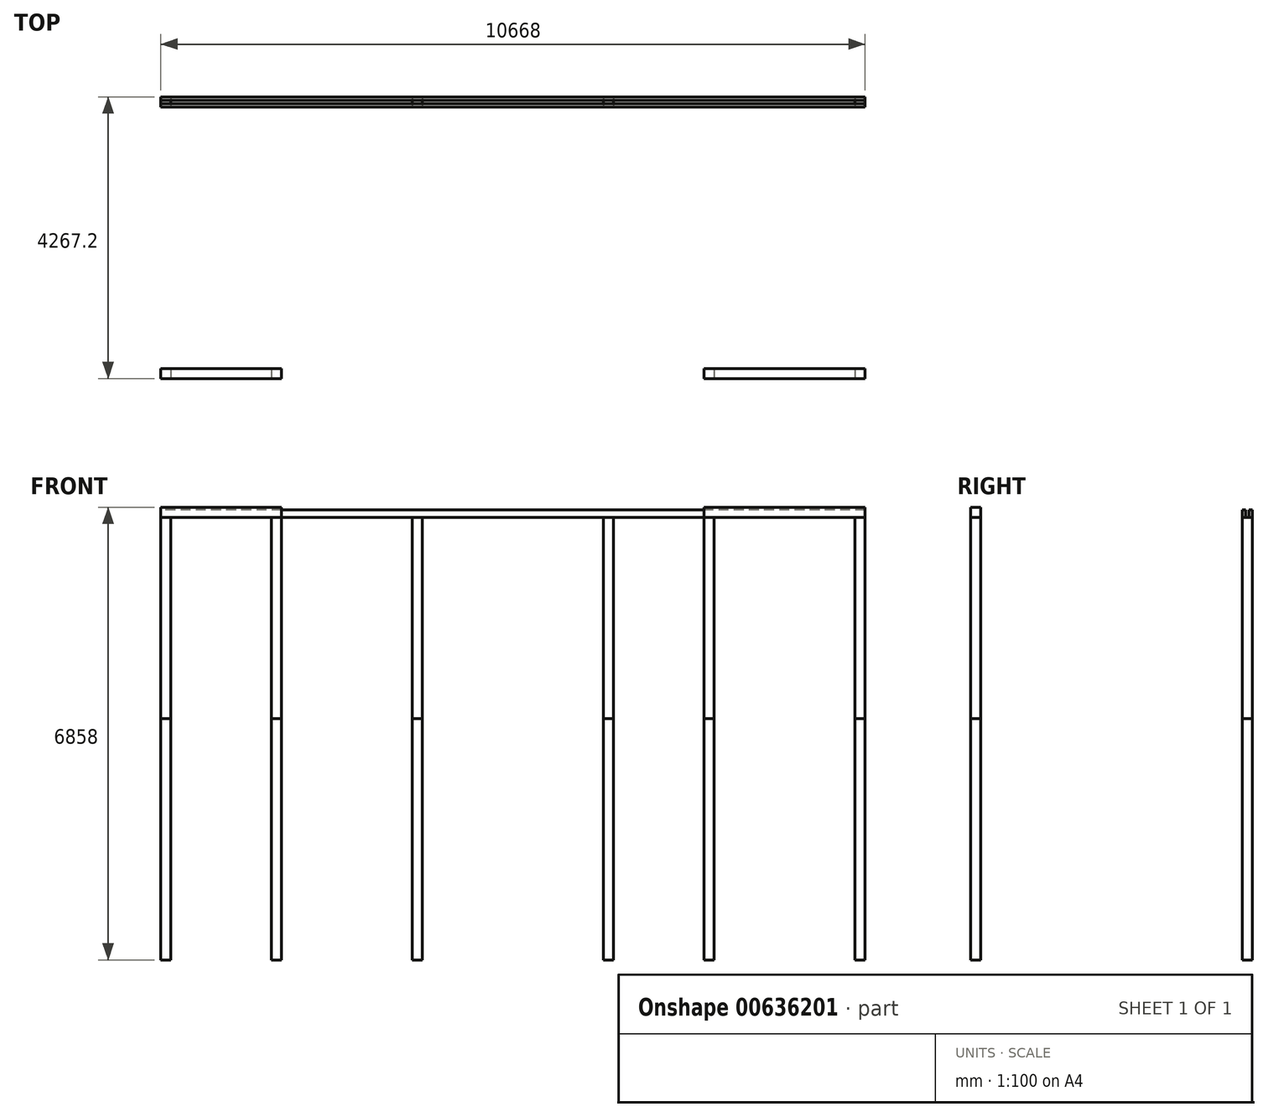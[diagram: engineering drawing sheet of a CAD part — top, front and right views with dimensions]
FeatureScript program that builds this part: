
annotation { "Feature Type Name" : "Feature", "Feature Type Description" : "" }
export const myFeature = defineFeature(function(context is Context, id is Id, definition is map)
    precondition{}
    {
        {
            var Q0;
            Q0=qCreatedBy(makeId("Top.planeOp"),FACE);
            var sketch = newSketch(context, id + "F0", { "sketchPlane" : qUnion([Q0])});
            skLineSegment(sketch, "E0.bottom", {"start": v(-152.4, 4130.06) * mm, "end": v(0, 4130.06) * mm});
            skLineSegment(sketch, "E0.top", {"start": v(-152.4, 3977.66) * mm, "end": v(0, 3977.66) * mm});
            skLineSegment(sketch, "E0.left", {"start": v(-152.4, 4130.06) * mm, "end": v(-152.4, 3977.66) * mm});
            skLineSegment(sketch, "E0.right", {"start": v(0, 4130.06) * mm, "end": v(0, 3977.66) * mm});
            skLineSegment(sketch, "E1.bottom", {"start": v(3657.6, 4130.06) * mm, "end": v(3810, 4130.06) * mm});
            skLineSegment(sketch, "E1.top", {"start": v(3657.6, 3977.66) * mm, "end": v(3810, 3977.66) * mm});
            skLineSegment(sketch, "E1.left", {"start": v(3657.6, 4130.06) * mm, "end": v(3657.6, 3977.66) * mm});
            skLineSegment(sketch, "E1.right", {"start": v(3810, 4130.06) * mm, "end": v(3810, 3977.66) * mm});
            skLineSegment(sketch, "E2.bottom", {"start": v(6553.2, 4130.06) * mm, "end": v(6705.6, 4130.06) * mm});
            skLineSegment(sketch, "E2.top", {"start": v(6553.2, 3977.66) * mm, "end": v(6705.6, 3977.66) * mm});
            skLineSegment(sketch, "E2.left", {"start": v(6553.2, 4130.06) * mm, "end": v(6553.2, 3977.66) * mm});
            skLineSegment(sketch, "E2.right", {"start": v(6705.6, 4130.06) * mm, "end": v(6705.6, 3977.66) * mm});
            skLineSegment(sketch, "E3.bottom", {"start": v(-152.4, 15.26) * mm, "end": v(0, 15.26) * mm});
            skLineSegment(sketch, "E3.top", {"start": v(-152.4, -137.14) * mm, "end": v(0, -137.14) * mm});
            skLineSegment(sketch, "E3.left", {"start": v(-152.4, 15.26) * mm, "end": v(-152.4, -137.14) * mm});
            skLineSegment(sketch, "E3.right", {"start": v(0, 15.26) * mm, "end": v(0, -137.14) * mm});
            skLineSegment(sketch, "E4.bottom", {"start": v(1524, 15.26) * mm, "end": v(1676.4, 15.26) * mm});
            skLineSegment(sketch, "E4.top", {"start": v(1524, -137.14) * mm, "end": v(1676.4, -137.14) * mm});
            skLineSegment(sketch, "E4.left", {"start": v(1524, 15.26) * mm, "end": v(1524, -137.14) * mm});
            skLineSegment(sketch, "E4.right", {"start": v(1676.4, 15.26) * mm, "end": v(1676.4, -137.14) * mm});
            skLineSegment(sketch, "E5.bottom", {"start": v(8077.2, 15.26) * mm, "end": v(8229.6, 15.26) * mm});
            skLineSegment(sketch, "E5.top", {"start": v(8077.2, -137.14) * mm, "end": v(8229.6, -137.14) * mm});
            skLineSegment(sketch, "E5.left", {"start": v(8077.2, 15.26) * mm, "end": v(8077.2, -137.14) * mm});
            skLineSegment(sketch, "E5.right", {"start": v(8229.6, 15.26) * mm, "end": v(8229.6, -137.14) * mm});
            skLineSegment(sketch, "E6.bottom", {"start": v(10363.2, 4130.06) * mm, "end": v(10515.6, 4130.06) * mm});
            skLineSegment(sketch, "E6.top", {"start": v(10363.2, 3977.66) * mm, "end": v(10515.6, 3977.66) * mm});
            skLineSegment(sketch, "E6.left", {"start": v(10363.2, 4130.06) * mm, "end": v(10363.2, 3977.66) * mm});
            skLineSegment(sketch, "E6.right", {"start": v(10515.6, 4130.06) * mm, "end": v(10515.6, 3977.66) * mm});
            skLineSegment(sketch, "E7.bottom", {"start": v(10363.2, 15.26) * mm, "end": v(10515.6, 15.26) * mm});
            skLineSegment(sketch, "E7.top", {"start": v(10363.2, -137.14) * mm, "end": v(10515.6, -137.14) * mm});
            skLineSegment(sketch, "E7.left", {"start": v(10363.2, 15.26) * mm, "end": v(10363.2, -137.14) * mm});
            skLineSegment(sketch, "E7.right", {"start": v(10515.6, 15.26) * mm, "end": v(10515.6, -137.14) * mm});
            skSolve(sketch);
        }
        {
            var Q0;
            Q0 = qSketchRegion(id + "F0", true);
            extrude(context, id + "F1", {"entities" : qUnion([Q0]), "depth" : 3048 * mm, "offsetDistance" : 25.4 * mm});
        }
        {
            var Q0;
            Q0 = qSketchRegion(id + "F0", true);
            extrude(context, id + "F2", {"entities" : qUnion([Q0]), "oppositeDirection" : true, "depth" : 3657.6 * mm, "offsetDistance" : 25.4 * mm});
        }
        {
            var Q0;
            Q0=makeQuery(id+"F1.opExtrude","SWEPT_FACE",FACE,{"disambiguationData":[OSD([sQuery(id+"F0.wireOp",EDGE,"E3.left")])]});
            var sketch = newSketch(context, id + "F3", { "sketchPlane" : qUnion([Q0])});
            skLineSegment(sketch, "E8.bottom", {"start": v(-15.26, 3048) * mm, "end": v(137.14, 3048) * mm});
            skLineSegment(sketch, "E8.top", {"start": v(-15.26, 3200.4) * mm, "end": v(137.14, 3200.4) * mm});
            skLineSegment(sketch, "E8.left", {"start": v(-15.26, 3048) * mm, "end": v(-15.26, 3200.4) * mm});
            skLineSegment(sketch, "E8.right", {"start": v(137.14, 3048) * mm, "end": v(137.14, 3200.4) * mm});
            skLineSegment(sketch, "E9.bottom", {"start": v(-4129.63, 3048.56) * mm, "end": v(-4078.83, 3048.56) * mm});
            skLineSegment(sketch, "E9.top", {"start": v(-4129.63, 3162.86) * mm, "end": v(-4078.83, 3162.86) * mm});
            skLineSegment(sketch, "E9.left", {"start": v(-4129.63, 3048.56) * mm, "end": v(-4129.63, 3162.86) * mm});
            skLineSegment(sketch, "E9.right", {"start": v(-4078.83, 3048.56) * mm, "end": v(-4078.83, 3162.86) * mm});
            skLineSegment(sketch, "E10", {"start": v(-3977.66, 3048) * mm, "end": v(-3977.66, 3162.86) * mm});
            skLineSegment(sketch, "E11", {"start": v(-3977.66, 3162.86) * mm, "end": v(-4028.46, 3162.86) * mm});
            skLineSegment(sketch, "E12", {"start": v(-4028.46, 3162.86) * mm, "end": v(-4028.46, 3048) * mm});
            skLineSegment(sketch, "E13", {"start": v(-4028.46, 3048) * mm, "end": v(-3977.66, 3048) * mm});
            skSolve(sketch);
        }
        {
            var Q0;
            Q0=makeQuery(id+"F3.imprint","IMPRINT",FACE,{"disambiguationData":[TD([[makeQuery(id+"F3.imprint","IMPRINT",EDGE,{"derivedFrom":sQuery(id+"F3.wireOp",EDGE,"E8.bottom")}),1.0]])]});
            var Q1;
            Q1=makeQuery(id+"F1.opExtrude","SWEPT_FACE",FACE,{"disambiguationData":[OSD([sQuery(id+"F0.wireOp",EDGE,"E4.right")])]});
            extrude(context, id + "F4", {"entities" : qUnion([Q0]), "endBound" : BoundingType.UP_TO_SURFACE, "oppositeDirection" : true, "depth" : 25.4 * mm, "endBoundEntityFace" : qUnion([Q1]), "offsetDistance" : 25.4 * mm});
        }
        {
            var Q0;
            Q0=makeQuery(id+"F1.opExtrude","SWEPT_FACE",FACE,{"disambiguationData":[OSD([sQuery(id+"F0.wireOp",EDGE,"E7.right")])]});
            var sketch = newSketch(context, id + "F5", { "sketchPlane" : qUnion([Q0])});
            skLineSegment(sketch, "E14.0", {"start": v(-137.14, 3048) * mm, "end": v(-137.14, 3200.4) * mm});
            skLineSegment(sketch, "E15.0", {"start": v(15.26, 3200.4) * mm, "end": v(-137.14, 3200.4) * mm});
            skLineSegment(sketch, "E16.0", {"start": v(15.26, 3048) * mm, "end": v(15.26, 3200.4) * mm});
            skLineSegment(sketch, "E17.0", {"start": v(15.26, 3048) * mm, "end": v(-137.14, 3048) * mm});
            skSolve(sketch);
        }
        {
            var Q0;
            Q0=makeQuery(id+"F5.imprint","IMPRINT",FACE,{"disambiguationData":[TD([[makeQuery(id+"F5.imprint","IMPRINT",EDGE,{"derivedFrom":sQuery(id+"F5.wireOp",EDGE,"E14.0")}),-1.0]])]});
            var Q1;
            Q1=makeQuery(id+"F1.opExtrude","SWEPT_FACE",FACE,{"disambiguationData":[OSD([sQuery(id+"F0.wireOp",EDGE,"E5.left")])]});
            extrude(context, id + "F6", {"entities" : qUnion([Q0]), "endBound" : BoundingType.UP_TO_SURFACE, "oppositeDirection" : true, "depth" : 25.4 * mm, "endBoundEntityFace" : qUnion([Q1]), "offsetDistance" : 25.4 * mm});
        }
        {
            var Q0;
            Q0=makeQuery(id+"F3.imprint","IMPRINT",FACE,{"disambiguationData":[TD([[makeQuery(id+"F3.imprint","IMPRINT",EDGE,{"derivedFrom":sQuery(id+"F3.wireOp",EDGE,"E9.bottom")}),1.0]])]});
            var Q1;
            Q1=makeQuery(id+"F3.imprint","IMPRINT",FACE,{"disambiguationData":[TD([[makeQuery(id+"F3.imprint","IMPRINT",EDGE,{"derivedFrom":sQuery(id+"F3.wireOp",EDGE,"E10")}),1.0]])]});
            var Q2;
            Q2=makeQuery(id+"F1.opExtrude","SWEPT_FACE",FACE,{"disambiguationData":[OSD([sQuery(id+"F0.wireOp",EDGE,"E6.right")])]});
            extrude(context, id + "F7", {"entities" : qUnion([Q0, Q1]), "endBound" : BoundingType.UP_TO_SURFACE, "oppositeDirection" : true, "depth" : 25.4 * mm, "endBoundEntityFace" : qUnion([Q2]), "offsetDistance" : 25.4 * mm});
        }
    });
